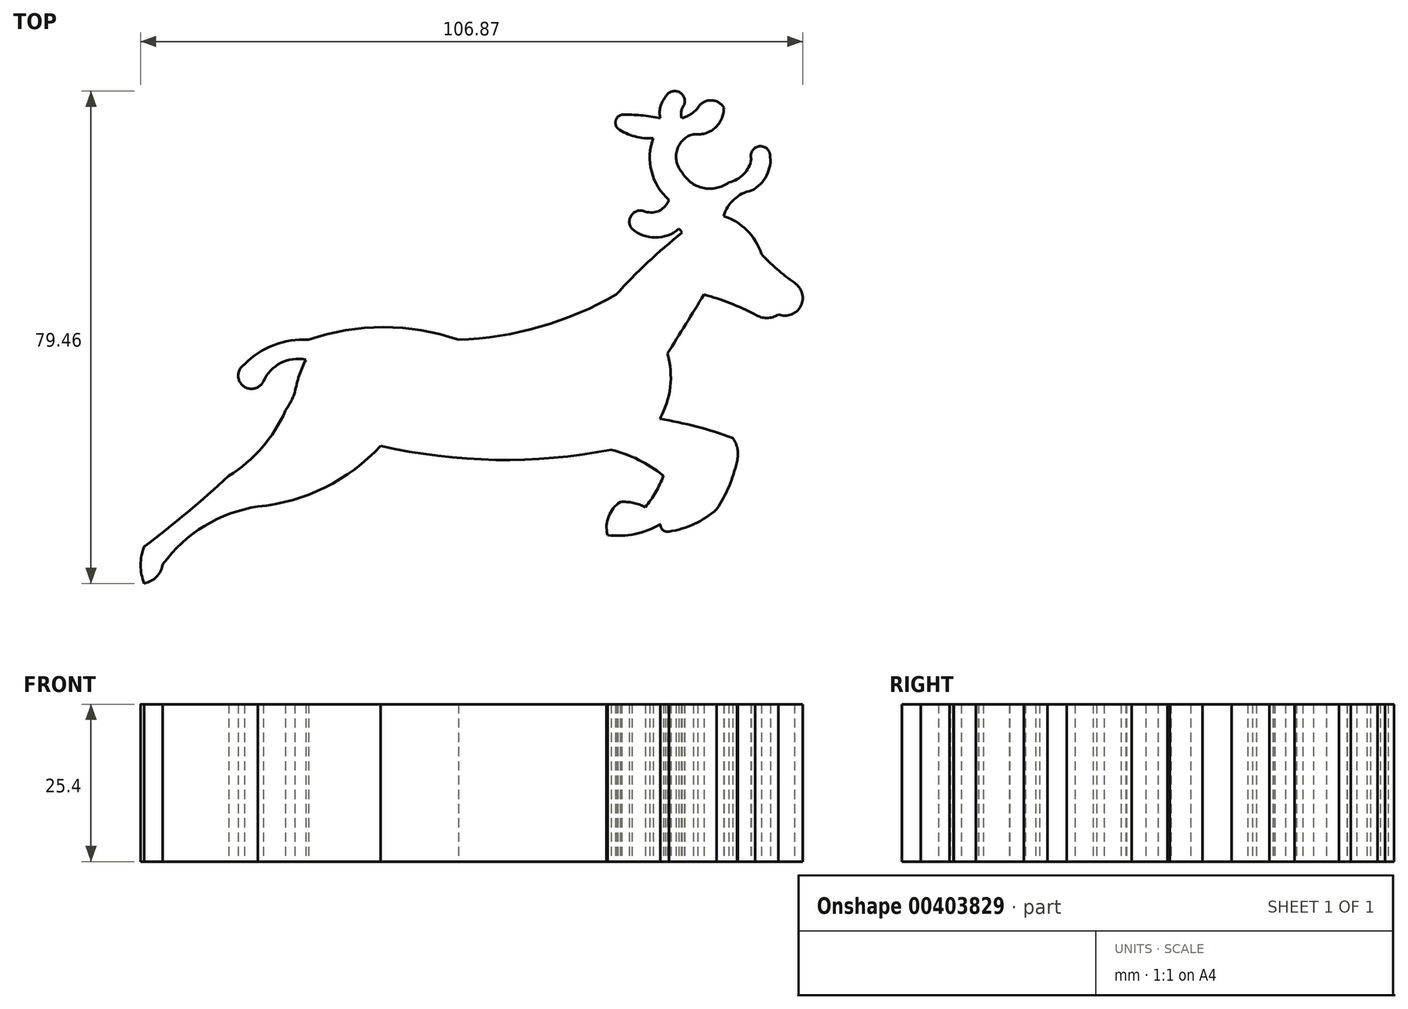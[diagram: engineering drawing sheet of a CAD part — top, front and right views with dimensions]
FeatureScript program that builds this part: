
annotation { "Feature Type Name" : "Feature", "Feature Type Description" : "" }
export const myFeature = defineFeature(function(context is Context, id is Id, definition is map)
    precondition{}
    {
        {
            var Q0;
            Q0=qCreatedBy(makeId("Top.planeOp"),FACE);
            var sketch = newSketch(context, id + "F0", { "sketchPlane" : qUnion([Q0])});
            skLineSegment(sketch, "E0", {"start": v(0, 0) * mm, "end": v(127, 0) * mm});
            skArc(sketch, "E1", {"start": v(33.85, -58.7) * mm, "mid": v(34.7, -57.29) * mm, "end": v(35.36, -55.77) * mm});
            skArc(sketch, "E2", {"start": v(37.11, -50.5) * mm, "mid": v(36.05, -53.07) * mm, "end": v(35.36, -55.77) * mm});
            skArc(sketch, "E3", {"start": v(37.11, -50.5) * mm, "mid": v(33.07, -51.06) * mm, "end": v(30.26, -54.02) * mm});
            skArc(sketch, "E4", {"start": v(27.22, -51.26) * mm, "mid": v(26.91, -54.66) * mm, "end": v(30.26, -54.02) * mm});
            skArc(sketch, "E5", {"start": v(37.58, -47.28) * mm, "mid": v(31.97, -48.14) * mm, "end": v(27.22, -51.26) * mm});
            skArc(sketch, "E6", {"start": v(11.04, -80.7) * mm, "mid": v(18, -75.15) * mm, "end": v(24.7, -69.28) * mm});
            skArc(sketch, "E7", {"start": v(11.04, -80.7) * mm, "mid": v(10.46, -83.66) * mm, "end": v(11.04, -86.62) * mm});
            skArc(sketch, "E8", {"start": v(11.04, -86.62) * mm, "mid": v(13.02, -85.56) * mm, "end": v(14.03, -83.55) * mm});
            skArc(sketch, "E9", {"start": v(29.36, -74.22) * mm, "mid": v(20.76, -77.35) * mm, "end": v(14.03, -83.55) * mm});
            skArc(sketch, "E10", {"start": v(29.36, -74.22) * mm, "mid": v(40.19, -71.15) * mm, "end": v(49.2, -64.41) * mm});
            skArc(sketch, "E11", {"start": v(49.2, -64.41) * mm, "mid": v(67.77, -66.69) * mm, "end": v(86.4, -65.05) * mm});
            skArc(sketch, "E12", {"start": v(61.73, -47.28) * mm, "mid": v(49.66, -45.27) * mm, "end": v(37.58, -47.28) * mm});
            skArc(sketch, "E13", {"start": v(61.73, -47.28) * mm, "mid": v(74.93, -45.21) * mm, "end": v(87.22, -40) * mm});
            skArc(sketch, "E14", {"start": v(97.81, -30.02) * mm, "mid": v(92.32, -34.8) * mm, "end": v(87.22, -40) * mm});
            skArc(sketch, "E15", {"start": v(110.64, -33.41) * mm, "mid": v(108.33, -29.64) * mm, "end": v(104.55, -27.32) * mm});
            skArc(sketch, "E16", {"start": v(110.64, -33.41) * mm, "mid": v(113.18, -35.9) * mm, "end": v(115.97, -38.1) * mm});
            skArc(sketch, "E17", {"start": v(113.4, -43.2) * mm, "mid": v(117.02, -41.83) * mm, "end": v(115.97, -38.1) * mm});
            skArc(sketch, "E18", {"start": v(109.65, -43.2) * mm, "mid": v(111.52, -43.78) * mm, "end": v(113.4, -43.2) * mm});
            skArc(sketch, "E19", {"start": v(109.65, -43.2) * mm, "mid": v(105.6, -41.39) * mm, "end": v(101.39, -40) * mm});
            skArc(sketch, "E20", {"start": v(95.48, -49.53) * mm, "mid": v(98.45, -44.77) * mm, "end": v(101.39, -40) * mm});
            skArc(sketch, "E21", {"start": v(94.25, -60.04) * mm, "mid": v(95.94, -54.91) * mm, "end": v(95.48, -49.53) * mm});
            skArc(sketch, "E22", {"start": v(106, -63.12) * mm, "mid": v(100.2, -61.32) * mm, "end": v(94.25, -60.04) * mm});
            skArc(sketch, "E23", {"start": v(94.83, -69.24) * mm, "mid": v(90.84, -66.68) * mm, "end": v(86.4, -65.05) * mm});
            skArc(sketch, "E24", {"start": v(98.07, -72.3) * mm, "mid": v(99.33, -70.14) * mm, "end": v(99.6, -67.64) * mm});
            skArc(sketch, "E25", {"start": v(100.23, -72.3) * mm, "mid": v(99.15, -72.23) * mm, "end": v(98.07, -72.3) * mm});
            skArc(sketch, "E26", {"start": v(100.23, -72.3) * mm, "mid": v(101.67, -69.76) * mm, "end": v(102.18, -66.88) * mm});
            skArc(sketch, "E27", {"start": v(91.91, -74.33) * mm, "mid": v(93.58, -71.9) * mm, "end": v(94.83, -69.24) * mm});
            skArc(sketch, "E28", {"start": v(91.91, -74.33) * mm, "mid": v(89.95, -73.62) * mm, "end": v(87.87, -73.49) * mm});
            skArc(sketch, "E29", {"start": v(87.87, -73.49) * mm, "mid": v(86, -75.82) * mm, "end": v(85.8, -78.8) * mm});
            skArc(sketch, "E30", {"start": v(85.8, -78.8) * mm, "mid": v(90.24, -78.66) * mm, "end": v(94.38, -77.04) * mm});
            skArc(sketch, "E31", {"start": v(94.38, -77.04) * mm, "mid": v(94.73, -78) * mm, "end": v(95.72, -78.25) * mm});
            skArc(sketch, "E32", {"start": v(95.72, -78.25) * mm, "mid": v(99.84, -77.02) * mm, "end": v(103.44, -74.68) * mm});
            skArc(sketch, "E33", {"start": v(106.7, -66.94) * mm, "mid": v(106.8, -64.95) * mm, "end": v(106, -63.12) * mm});
            skArc(sketch, "E34", {"start": v(103.44, -74.68) * mm, "mid": v(105.42, -70.96) * mm, "end": v(106.7, -66.94) * mm});
            skArc(sketch, "E35", {"start": v(109.03, -23.22) * mm, "mid": v(106.22, -24.65) * mm, "end": v(104.55, -27.32) * mm});
            skArc(sketch, "E36", {"start": v(97.81, -30.02) * mm, "mid": v(97.62, -29.67) * mm, "end": v(97.35, -29.38) * mm});
            skArc(sketch, "E37", {"start": v(109.03, -23.22) * mm, "mid": v(111.5, -20.78) * mm, "end": v(112.03, -17.35) * mm});
            skArc(sketch, "E38", {"start": v(112.03, -17.35) * mm, "mid": v(110.11, -16.1) * mm, "end": v(109.03, -18.12) * mm});
            skArc(sketch, "E39", {"start": v(89.74, -29.38) * mm, "mid": v(93.55, -30.8) * mm, "end": v(97.35, -29.38) * mm});
            skArc(sketch, "E40", {"start": v(91.91, -26.61) * mm, "mid": v(89.72, -27.13) * mm, "end": v(89.74, -29.38) * mm});
            skArc(sketch, "E41", {"start": v(91.91, -26.61) * mm, "mid": v(94.2, -26.44) * mm, "end": v(95.72, -24.73) * mm});
            skArc(sketch, "E42", {"start": v(105.4, -21.89) * mm, "mid": v(107.8, -20.56) * mm, "end": v(109.03, -18.12) * mm});
            skArc(sketch, "E43", {"start": v(97.82, -20.21) * mm, "mid": v(101.23, -22.8) * mm, "end": v(105.4, -21.89) * mm});
            skArc(sketch, "E44", {"start": v(99.69, -14.1) * mm, "mid": v(97.04, -16.64) * mm, "end": v(97.82, -20.21) * mm});
            skArc(sketch, "E45", {"start": v(93.21, -14.75) * mm, "mid": v(92.92, -20.13) * mm, "end": v(95.72, -24.73) * mm});
            skArc(sketch, "E46", {"start": v(99.69, -14.1) * mm, "mid": v(103.14, -13.12) * mm, "end": v(104.6, -9.84) * mm});
            skArc(sketch, "E47", {"start": v(104.6, -9.84) * mm, "mid": v(102.45, -8.65) * mm, "end": v(100.36, -9.93) * mm});
            skArc(sketch, "E48", {"start": v(97.82, -11.55) * mm, "mid": v(99.2, -10.92) * mm, "end": v(100.36, -9.93) * mm});
            skArc(sketch, "E49", {"start": v(98.2, -9.4) * mm, "mid": v(97.71, -10.42) * mm, "end": v(97.82, -11.55) * mm});
            skArc(sketch, "E50", {"start": v(98.2, -9.4) * mm, "mid": v(97.3, -7.3) * mm, "end": v(95.16, -8.11) * mm});
            skArc(sketch, "E51", {"start": v(95.16, -8.11) * mm, "mid": v(94.35, -9.73) * mm, "end": v(94.33, -11.55) * mm});
            skArc(sketch, "E52", {"start": v(24.7, -69.28) * mm, "mid": v(30.08, -64.69) * mm, "end": v(33.85, -58.7) * mm});
            skPoint(sketch, "E53.end.orphan", {"position": v(12.36, -74.22) * mm});
            skArc(sketch, "E54", {"start": v(94.33, -11.55) * mm, "mid": v(91.24, -11.08) * mm, "end": v(88.12, -10.98) * mm});
            skArc(sketch, "E55", {"start": v(87.48, -13.2) * mm, "mid": v(90.2, -14.48) * mm, "end": v(93.21, -14.75) * mm});
            skArc(sketch, "E56", {"start": v(88.12, -10.98) * mm, "mid": v(87.14, -11.9) * mm, "end": v(87.48, -13.2) * mm});
            skArc(sketch, "E57", {"start": v(96.16, -65.05) * mm, "mid": v(91.27, -64.86) * mm, "end": v(86.4, -65.05) * mm});
            skArc(sketch, "E58", {"start": v(98.07, -72.3) * mm, "mid": v(95.3, -73.94) * mm, "end": v(94.38, -77.04) * mm});
            skSolve(sketch);
        }
        {
            var Q0;
            Q0 = qSketchRegion(id + "F0", true);
            extrude(context, id + "F1", {"entities" : qUnion([Q0]), "depth" : 25.4 * mm});
        }
    });
